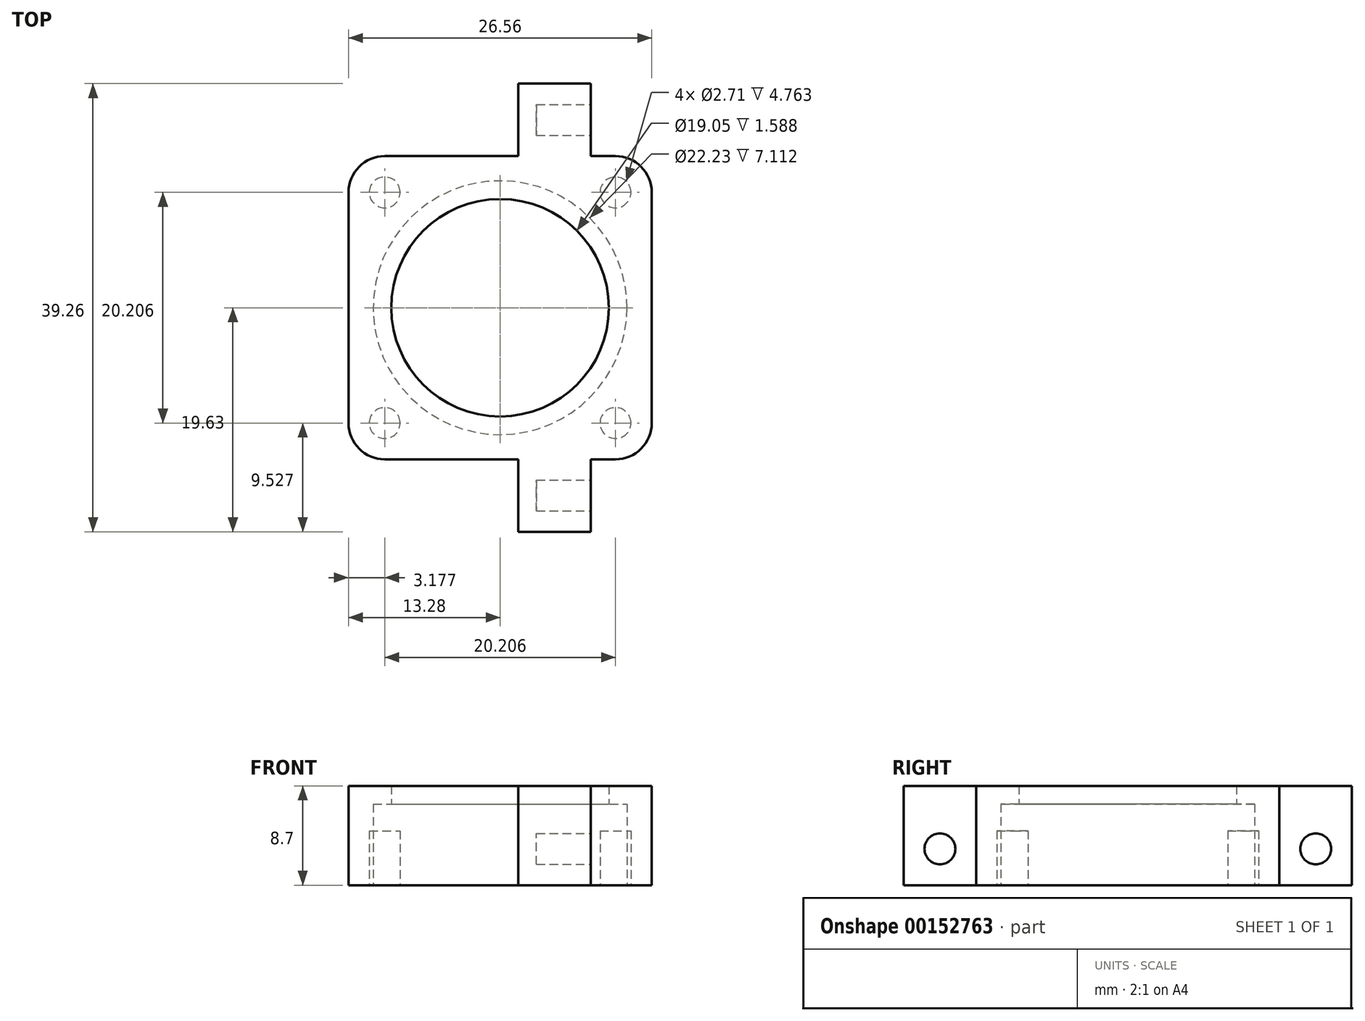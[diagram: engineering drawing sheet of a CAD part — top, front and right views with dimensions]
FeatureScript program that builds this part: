
annotation { "Feature Type Name" : "Feature", "Feature Type Description" : "" }
export const myFeature = defineFeature(function(context is Context, id is Id, definition is map)
    precondition{}
    {
        {
            var Q0;
            Q0=qCreatedBy(makeId("Top.planeOp"),FACE);
            var sketch = newSketch(context, id + "F0", { "sketchPlane" : qUnion([Q0])});
            skCircle(sketch, "E0", {"center": v(0, 0) * mm, "radius": 11.11 * mm, "construction": true});
            skLineSegment(sketch, "E1", {"start": v(0, 0) * mm, "end": v(0, -13.28) * mm, "construction": true});
            skLineSegment(sketch, "E2.bottom", {"start": v(13.28, -13.28) * mm, "end": v(-13.28, -13.28) * mm});
            skLineSegment(sketch, "E2.top", {"start": v(13.28, 13.28) * mm, "end": v(-13.28, 13.28) * mm});
            skLineSegment(sketch, "E2.left", {"start": v(13.28, -13.28) * mm, "end": v(13.28, 13.28) * mm});
            skLineSegment(sketch, "E2.right", {"start": v(-13.28, -13.28) * mm, "end": v(-13.28, 13.28) * mm});
            skLineSegment(sketch, "E3.bottom", {"start": v(-10.1, 10.1) * mm, "end": v(10.1, 10.1) * mm, "construction": true});
            skLineSegment(sketch, "E3.top", {"start": v(-10.1, -10.1) * mm, "end": v(10.1, -10.1) * mm, "construction": true});
            skLineSegment(sketch, "E3.left", {"start": v(-10.1, 10.1) * mm, "end": v(-10.1, -10.1) * mm, "construction": true});
            skLineSegment(sketch, "E3.right", {"start": v(10.1, 10.1) * mm, "end": v(10.1, -10.1) * mm, "construction": true});
            skCircle(sketch, "E4", {"center": v(-10.1, 10.1) * mm, "radius": 3.18 * mm, "construction": true});
            skLineSegment(sketch, "E5", {"start": v(0, 0) * mm, "end": v(0, 13.28) * mm, "construction": true});
            skCircle(sketch, "E6", {"center": v(-10.1, 10.1) * mm, "radius": 1.83 * mm, "construction": true});
            skCircle(sketch, "E7", {"center": v(10.1, 10.1) * mm, "radius": 1.83 * mm, "construction": true});
            skCircle(sketch, "E8", {"center": v(10.1, -10.1) * mm, "radius": 1.83 * mm, "construction": true});
            skCircle(sketch, "E9", {"center": v(-10.1, -10.1) * mm, "radius": 1.83 * mm, "construction": true});
            skCircle(sketch, "E10", {"center": v(0, 0) * mm, "radius": 9.53 * mm});
            skSolve(sketch);
        }
        {
            var Q0;
            Q0=qSketchRegion(id+"F0",true);
            extrude(context, id + "F1", {"entities" : qUnion([Q0]), "depth" : 8.7 * mm});
        }
        {
            var Q0;
            Q0=makeQuery(id+"F1.opExtrude","SWEPT_EDGE",EDGE,{"disambiguationData":[OSD([sQuery(id+"F0.wireOp",EDGE,"E2.top"),sQuery(id+"F0.wireOp",EDGE,"E2.right")])]});
            var Q1;
            Q1=makeQuery(id+"F1.opExtrude","SWEPT_EDGE",EDGE,{"disambiguationData":[OSD([sQuery(id+"F0.wireOp",EDGE,"E2.bottom"),sQuery(id+"F0.wireOp",EDGE,"E2.right")])]});
            var Q2;
            Q2=makeQuery(id+"F1.opExtrude","SWEPT_EDGE",EDGE,{"disambiguationData":[OSD([sQuery(id+"F0.wireOp",EDGE,"E2.bottom"),sQuery(id+"F0.wireOp",EDGE,"E2.left")])]});
            var Q3;
            Q3=makeQuery(id+"F1.opExtrude","SWEPT_EDGE",EDGE,{"disambiguationData":[OSD([sQuery(id+"F0.wireOp",EDGE,"E2.top"),sQuery(id+"F0.wireOp",EDGE,"E2.left")])]});
            fillet(context, id + "F2", {"entities" : qUnion([Q0, Q1, Q2, Q3]), "radius" : 3.17 * mm, "tangentPropagation" : true, "allowEdgeOverflow" : false});
        }
        {
            var Q0;
            Q0=makeQuery(id+"F1.opExtrude","CAP_FACE",FACE,{"disambiguationData":[OSD([sQuery(id+"F0.wireOp",EDGE,"E2.bottom"),sQuery(id+"F0.wireOp",EDGE,"E2.top"),sQuery(id+"F0.wireOp",EDGE,"E2.left"),sQuery(id+"F0.wireOp",EDGE,"E2.right"),sQuery(id+"F0.wireOp",EDGE,"E6"),sQuery(id+"F0.wireOp",EDGE,"E7"),sQuery(id+"F0.wireOp",EDGE,"E8"),sQuery(id+"F0.wireOp",EDGE,"E9"),sQuery(id+"F0.wireOp",EDGE,"E10")])],"isStart":true});
            var sketch = newSketch(context, id + "F3", { "sketchPlane" : qUnion([Q0])});
            skCircle(sketch, "E11", {"center": v(0, 0) * mm, "radius": 11.11 * mm});
            skSolve(sketch);
        }
        {
            var Q0;
            Q0=qSketchRegion(id+"F3",true);
            extrude(context, id + "F4", {"entities" : qUnion([Q0]), "operationType" : NewBodyOperationType.REMOVE, "oppositeDirection" : true, "depth" : 7.11 * mm});
        }
        {
            var Q0;
            Q0=makeQuery(id+"F1.opExtrude","CAP_FACE",FACE,{"disambiguationData":[OSD([sQuery(id+"F0.wireOp",EDGE,"E2.bottom"),sQuery(id+"F0.wireOp",EDGE,"E2.top"),sQuery(id+"F0.wireOp",EDGE,"E2.left"),sQuery(id+"F0.wireOp",EDGE,"E2.right"),sQuery(id+"F0.wireOp",EDGE,"E10")])],"isStart":true});
            var sketch = newSketch(context, id + "F5", { "sketchPlane" : qUnion([Q0])});
            skCircle(sketch, "E12", {"center": v(10.1, 10.1) * mm, "radius": 1.35 * mm});
            skCircle(sketch, "E13", {"center": v(-10.1, 10.1) * mm, "radius": 1.35 * mm});
            skCircle(sketch, "E14", {"center": v(-10.1, -10.1) * mm, "radius": 1.35 * mm});
            skCircle(sketch, "E15", {"center": v(10.1, -10.1) * mm, "radius": 1.35 * mm});
            skSolve(sketch);
        }
        {
            var Q0;
            Q0=qSketchRegion(id+"F5",true);
            extrude(context, id + "F6", {"entities" : qUnion([Q0]), "operationType" : NewBodyOperationType.REMOVE, "oppositeDirection" : true, "depth" : 4.76 * mm});
        }
        {
            var Q0;
            Q0=makeQuery(id+"F1.opExtrude","CAP_FACE",FACE,{"disambiguationData":[OSD([sQuery(id+"F0.wireOp",EDGE,"E2.bottom"),sQuery(id+"F0.wireOp",EDGE,"E2.top"),sQuery(id+"F0.wireOp",EDGE,"E2.left"),sQuery(id+"F0.wireOp",EDGE,"E2.right"),sQuery(id+"F0.wireOp",EDGE,"E10")])],"isStart":false});
            var sketch = newSketch(context, id + "F7", { "sketchPlane" : qUnion([Q0])});
            skLineSegment(sketch, "E16.bottom", {"start": v(7.94, -13.28) * mm, "end": v(1.59, -13.28) * mm});
            skLineSegment(sketch, "E16.top", {"start": v(7.94, -19.63) * mm, "end": v(1.59, -19.63) * mm});
            skLineSegment(sketch, "E16.left", {"start": v(7.94, -13.28) * mm, "end": v(7.94, -19.63) * mm});
            skLineSegment(sketch, "E16.right", {"start": v(1.59, -13.28) * mm, "end": v(1.59, -19.63) * mm});
            skLineSegment(sketch, "E17.bottom", {"start": v(7.94, 13.28) * mm, "end": v(1.59, 13.28) * mm});
            skLineSegment(sketch, "E17.top", {"start": v(7.94, 19.63) * mm, "end": v(1.59, 19.63) * mm});
            skLineSegment(sketch, "E17.left", {"start": v(7.94, 13.28) * mm, "end": v(7.94, 19.63) * mm});
            skLineSegment(sketch, "E17.right", {"start": v(1.59, 13.28) * mm, "end": v(1.59, 19.63) * mm});
            skLineSegment(sketch, "E18", {"start": v(4.76, -13.28) * mm, "end": v(4.76, 13.28) * mm, "construction": true});
            skLineSegment(sketch, "E19", {"start": v(4.76, 0) * mm, "end": v(0, 0) * mm, "construction": true});
            skSolve(sketch);
        }
        {
            var Q0;
            Q0 = qSketchRegion(id + "F7", true);
            var Q1;
            Q1=makeQuery(id+"F1.opExtrude","CAP_FACE",FACE,{"disambiguationData":[OSD([sQuery(id+"F0.wireOp",EDGE,"E2.bottom"),sQuery(id+"F0.wireOp",EDGE,"E2.top"),sQuery(id+"F0.wireOp",EDGE,"E2.left"),sQuery(id+"F0.wireOp",EDGE,"E2.right"),sQuery(id+"F0.wireOp",EDGE,"E10")])],"isStart":true});
            extrude(context, id + "F8", {"entities" : qUnion([Q0]), "operationType" : NewBodyOperationType.ADD, "endBound" : BoundingType.UP_TO_SURFACE, "oppositeDirection" : true, "endBoundEntityFace" : qUnion([Q1]), "depth" : 25.4 * mm});
        }
        {
            var Q0;
            Q0=makeQuery(id+"F8.opExtrude","SWEPT_FACE",FACE,{"disambiguationData":[OSD([sQuery(id+"F7.wireOp",EDGE,"E16.left")])]});
            var sketch = newSketch(context, id + "F9", { "sketchPlane" : qUnion([Q0])});
            skLineSegment(sketch, "E20.bottom", {"start": v(-16.45, 0) * mm, "end": v(-19.63, 0) * mm, "construction": true});
            skLineSegment(sketch, "E20.top", {"start": v(-16.45, 3.17) * mm, "end": v(-19.63, 3.17) * mm, "construction": true});
            skLineSegment(sketch, "E20.left", {"start": v(-16.45, 0) * mm, "end": v(-16.45, 3.17) * mm, "construction": true});
            skLineSegment(sketch, "E20.right", {"start": v(-19.63, 0) * mm, "end": v(-19.63, 3.17) * mm, "construction": true});
            skLineSegment(sketch, "E21.bottom", {"start": v(16.45, 0) * mm, "end": v(19.63, 0) * mm, "construction": true});
            skLineSegment(sketch, "E21.top", {"start": v(16.45, 3.18) * mm, "end": v(19.63, 3.18) * mm, "construction": true});
            skLineSegment(sketch, "E21.left", {"start": v(16.45, 0) * mm, "end": v(16.45, 3.18) * mm, "construction": true});
            skLineSegment(sketch, "E21.right", {"start": v(19.63, 0) * mm, "end": v(19.63, 3.18) * mm, "construction": true});
            skCircle(sketch, "E22", {"center": v(16.45, 3.18) * mm, "radius": 1.35 * mm});
            skCircle(sketch, "E23", {"center": v(-16.45, 3.17) * mm, "radius": 1.35 * mm});
            skSolve(sketch);
        }
        {
            var Q0;
            Q0 = qSketchRegion(id + "F9", true);
            extrude(context, id + "F10", {"entities" : qUnion([Q0]), "operationType" : NewBodyOperationType.REMOVE, "oppositeDirection" : true, "depth" : 4.76 * mm});
        }
    });
